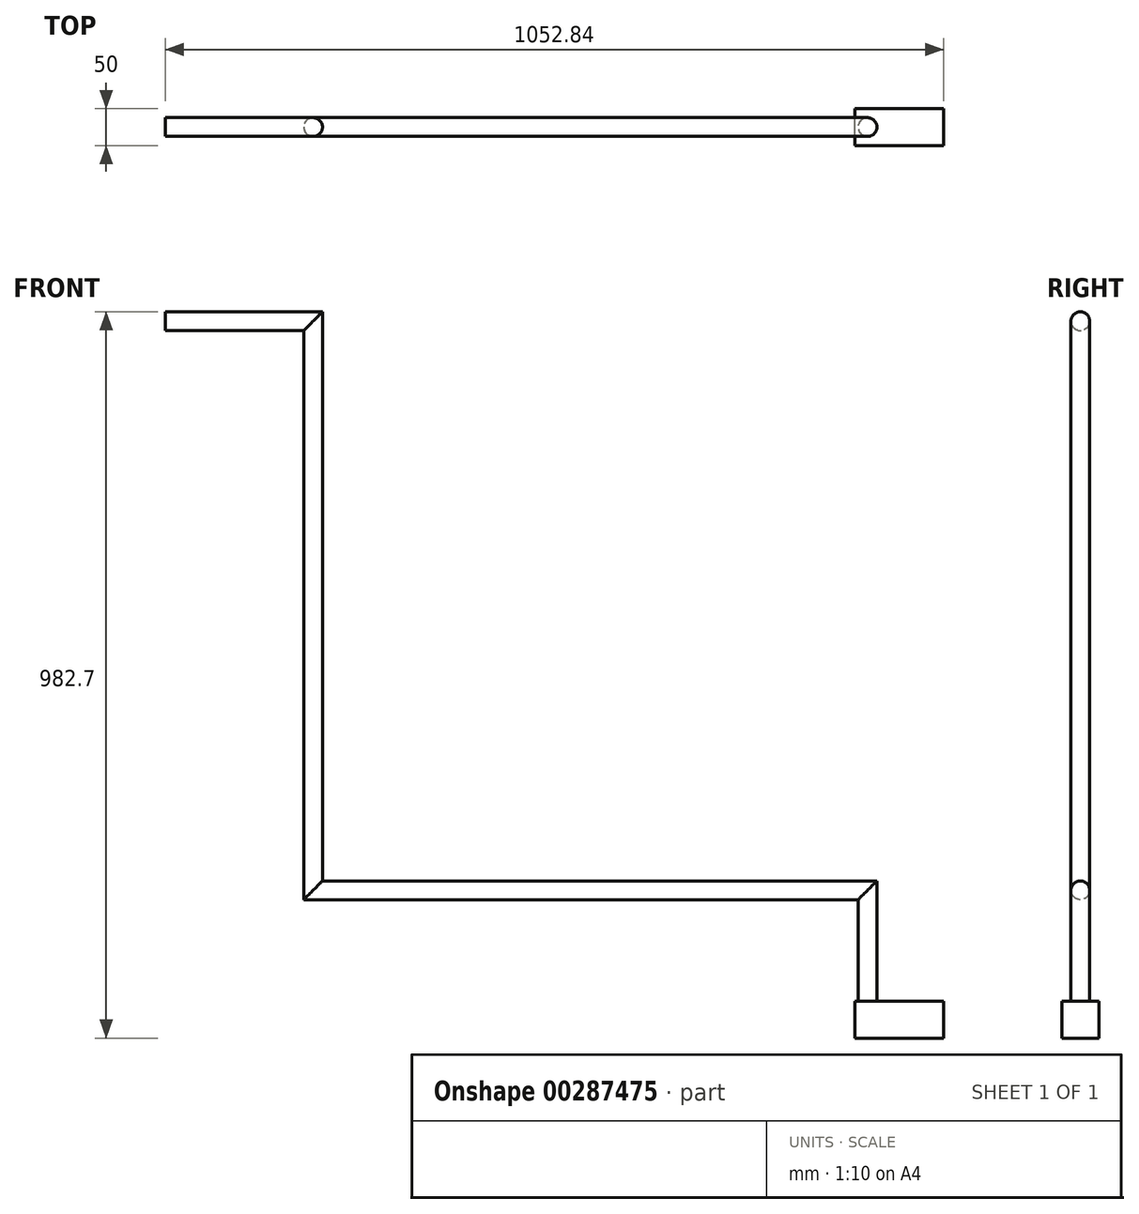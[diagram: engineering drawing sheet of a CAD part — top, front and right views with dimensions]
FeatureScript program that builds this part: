
annotation { "Feature Type Name" : "Feature", "Feature Type Description" : "" }
export const myFeature = defineFeature(function(context is Context, id is Id, definition is map)
    precondition{}
    {
        {
            var Q0;
            Q0=qCreatedBy(makeId("Front.planeOp"),FACE);
            var sketch = newSketch(context, id + "F0", { "sketchPlane" : qUnion([Q0])});
            skLineSegment(sketch, "E0.bottom", {"start": v(-17.16, 0) * mm, "end": v(102.84, 0) * mm});
            skLineSegment(sketch, "E0.top", {"start": v(-17.16, -50) * mm, "end": v(102.84, -50) * mm});
            skLineSegment(sketch, "E0.left", {"start": v(-17.16, 0) * mm, "end": v(-17.16, -50) * mm});
            skLineSegment(sketch, "E0.right", {"start": v(102.84, 0) * mm, "end": v(102.84, -50) * mm});
            skSolve(sketch);
        }
        {
            var Q0;
            Q0=qSketchRegion(id+"F0",true);
            extrude(context, id + "F1", {"entities" : qUnion([Q0]), "depth" : 25 * mm, "hasSecondDirection" : true, "secondDirectionOppositeDirection" : true, "secondDirectionDepth" : 25 * mm});
        }
        {
            var Q0;
            Q0=qCreatedBy(makeId("Front.planeOp"),FACE);
            var sketch = newSketch(context, id + "F2", { "sketchPlane" : qUnion([Q0])});
            skLineSegment(sketch, "E1", {"start": v(0, 0) * mm, "end": v(0, 150) * mm});
            skLineSegment(sketch, "E2", {"start": v(0, 150) * mm, "end": v(-750, 150) * mm});
            skLineSegment(sketch, "E3", {"start": v(-750, 150) * mm, "end": v(-750, 920) * mm});
            skLineSegment(sketch, "E4", {"start": v(-750, 920) * mm, "end": v(-950, 920) * mm});
            skSolve(sketch);
        }
        {
            var Q0;
            Q0=qCreatedBy(makeId("Top.planeOp"),FACE);
            var sketch = newSketch(context, id + "F3", { "sketchPlane" : qUnion([Q0])});
            skCircle(sketch, "E5", {"center": v(0, 0) * mm, "radius": 12.7 * mm});
            skSolve(sketch);
        }
        {
            var Q0;
            Q0=makeQuery(id+"F3.imprint","IMPRINT",FACE,{"disambiguationData":[TD([[makeQuery(id+"F3.imprint","IMPRINT",EDGE,{"derivedFrom":sQuery(id+"F3.wireOp",EDGE,"E5")}),1.0]])]});
            var Q1;
            Q1=sQuery(id+"F2.wireOp",EDGE,"E2");
            var Q2;
            Q2=sQuery(id+"F2.wireOp",EDGE,"E1");
            var Q3;
            Q3=sQuery(id+"F2.wireOp",EDGE,"E3");
            var Q4;
            Q4=sQuery(id+"F2.wireOp",EDGE,"E4");
            sweep(context, id + "F4", {"operationType" : NewBodyOperationType.ADD, "profiles" : qUnion([Q0]), "path" : qUnion([Q1, Q2, Q3, Q4])});
        }
    });
